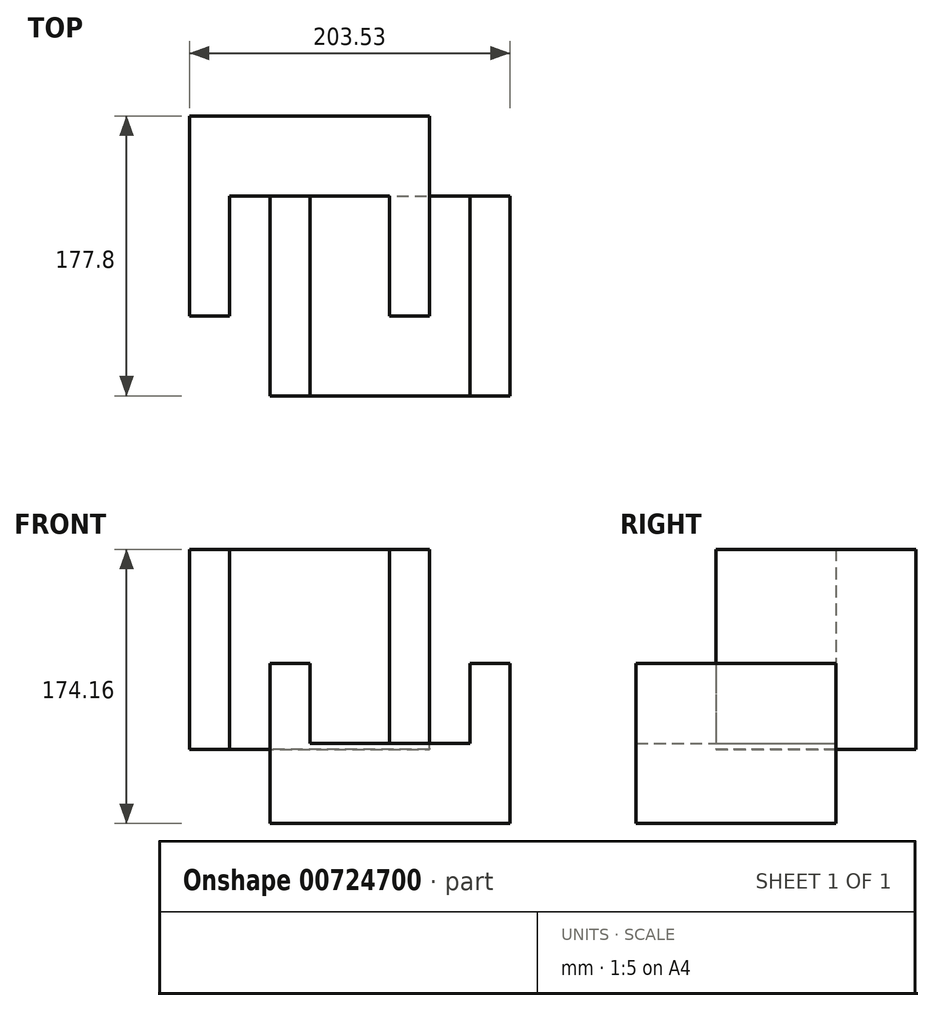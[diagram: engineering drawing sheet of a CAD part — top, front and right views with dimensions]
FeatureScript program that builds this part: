
annotation { "Feature Type Name" : "Feature", "Feature Type Description" : "" }
export const myFeature = defineFeature(function(context is Context, id is Id, definition is map)
    precondition{}
    {
        {
            var Q0;
            Q0=qCreatedBy(makeId("Front.planeOp"),FACE);
            var sketch = newSketch(context, id + "F0", { "sketchPlane" : qUnion([Q0])});
            skLineSegment(sketch, "E0", {"start": v(-89.8, -47.16) * mm, "end": v(62.6, -47.16) * mm});
            skLineSegment(sketch, "E1", {"start": v(62.6, -47.16) * mm, "end": v(62.6, 54.44) * mm});
            skLineSegment(sketch, "E2", {"start": v(62.6, 54.44) * mm, "end": v(37.2, 54.44) * mm});
            skLineSegment(sketch, "E3", {"start": v(37.2, 54.44) * mm, "end": v(37.2, 3.64) * mm});
            skLineSegment(sketch, "E4", {"start": v(37.2, 3.64) * mm, "end": v(-64.4, 3.64) * mm});
            skLineSegment(sketch, "E5", {"start": v(-64.4, 3.64) * mm, "end": v(-64.4, 54.44) * mm});
            skLineSegment(sketch, "E6", {"start": v(-64.4, 54.44) * mm, "end": v(-89.8, 54.44) * mm});
            skLineSegment(sketch, "E7", {"start": v(-89.8, 54.44) * mm, "end": v(-89.8, -47.16) * mm});
            skSolve(sketch);
        }
        {
            var Q0;
            Q0 = qSketchRegion(id + "F0", true);
            extrude(context, id + "F1", {"entities" : qUnion([Q0]), "depth" : 127 * mm, "offsetDistance" : 25.4 * mm});
        }
        {
            var Q0;
            Q0=qCreatedBy(makeId("Top.planeOp"),FACE);
            var sketch = newSketch(context, id + "F2", { "sketchPlane" : qUnion([Q0])});
            skLineSegment(sketch, "E8", {"start": v(-140.92, 50.8) * mm, "end": v(11.48, 50.8) * mm});
            skLineSegment(sketch, "E9", {"start": v(11.48, 50.8) * mm, "end": v(11.48, -76.2) * mm});
            skLineSegment(sketch, "E10", {"start": v(11.48, -76.2) * mm, "end": v(-13.92, -76.2) * mm});
            skLineSegment(sketch, "E11", {"start": v(-13.92, -76.2) * mm, "end": v(-13.92, 0) * mm});
            skLineSegment(sketch, "E12", {"start": v(-13.92, 0) * mm, "end": v(-115.52, 0) * mm});
            skLineSegment(sketch, "E13", {"start": v(-115.52, 0) * mm, "end": v(-115.52, -76.2) * mm});
            skLineSegment(sketch, "E14", {"start": v(-115.52, -76.2) * mm, "end": v(-140.92, -76.2) * mm});
            skLineSegment(sketch, "E15", {"start": v(-140.92, -76.2) * mm, "end": v(-140.92, 50.8) * mm});
            skSolve(sketch);
        }
        {
            var Q0;
            Q0 = qSketchRegion(id + "F2", true);
            extrude(context, id + "F3", {"entities" : qUnion([Q0]), "operationType" : NewBodyOperationType.ADD, "depth" : 127 * mm, "offsetDistance" : 25.4 * mm});
        }
    });
